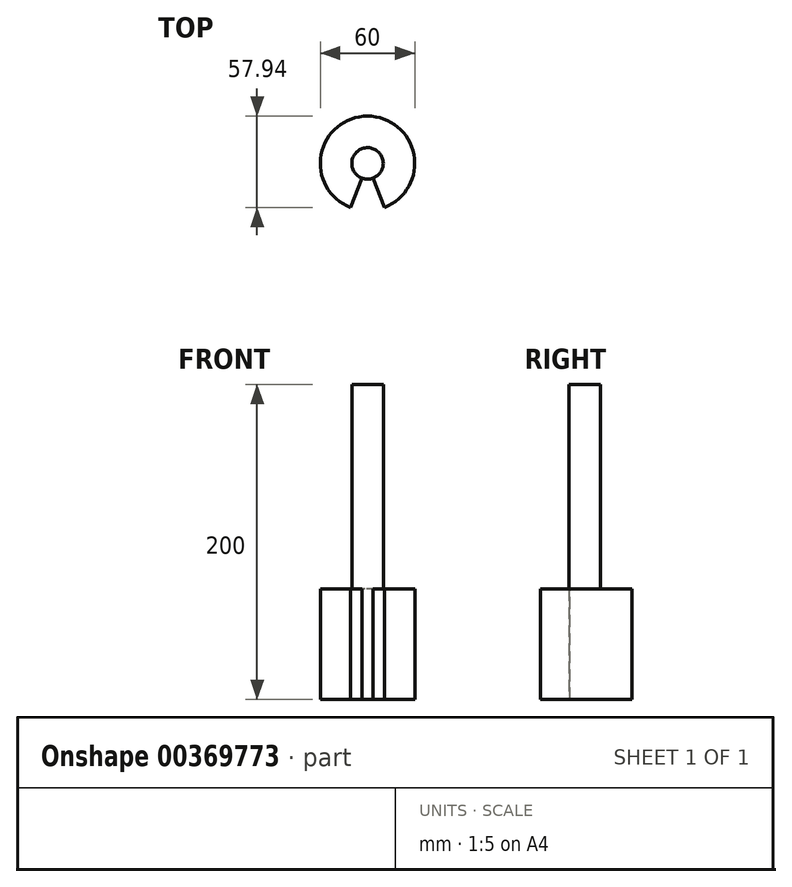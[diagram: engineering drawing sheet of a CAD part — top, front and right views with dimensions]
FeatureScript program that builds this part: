
annotation { "Feature Type Name" : "Feature", "Feature Type Description" : "" }
export const myFeature = defineFeature(function(context is Context, id is Id, definition is map)
    precondition{}
    {
        {
            var Q0;
            Q0=qCreatedBy(makeId("Top.planeOp"),FACE);
            var sketch = newSketch(context, id + "F0", { "sketchPlane" : qUnion([Q0])});
            skCircle(sketch, "E0", {"center": v(0, 0) * mm, "radius": 30 * mm});
            skCircle(sketch, "E1", {"center": v(0, 0) * mm, "radius": 10 * mm});
            skSolve(sketch);
        }
        {
            var Q0;
            Q0=makeQuery(id+"F0.imprint","IMPRINT",FACE,{"disambiguationData":[TD([[makeQuery(id+"F0.imprint","IMPRINT",EDGE,{"derivedFrom":sQuery(id+"F0.wireOp",EDGE,"E0")}),1.0]])]});
            extrude(context, id + "F1", {"entities" : qUnion([Q0]), "depth" : 70 * mm, "offsetDistance" : 25 * mm});
        }
        {
            var Q0;
            Q0=makeQuery(id+"F1.opExtrude","CAP_FACE",FACE,{"disambiguationData":[OSD([sQuery(id+"F0.wireOp",EDGE,"E0")])],"isStart":false});
            var sketch = newSketch(context, id + "F2", { "sketchPlane" : qUnion([Q0])});
            skCircle(sketch, "E2", {"center": v(0, 0) * mm, "radius": 10 * mm});
            skSolve(sketch);
        }
        {
            var Q0;
            Q0=makeQuery(id+"F2.imprint","IMPRINT",FACE,{"disambiguationData":[TD([[makeQuery(id+"F2.imprint","IMPRINT",EDGE,{"derivedFrom":sQuery(id+"F2.wireOp",EDGE,"E2")}),1.0]])]});
            extrude(context, id + "F3", {"entities" : qUnion([Q0]), "operationType" : NewBodyOperationType.ADD, "depth" : 130 * mm, "offsetDistance" : 25 * mm, "hasSecondDirection" : true, "secondDirectionOppositeDirection" : true, "secondDirectionDepth" : 70 * mm});
        }
        {
            var Q0;
            Q0=makeQuery(id+"F1.opExtrude","CAP_FACE",FACE,{"disambiguationData":[OSD([sQuery(id+"F0.wireOp",EDGE,"E0"),sQuery(id+"F0.wireOp",EDGE,"E1")])],"isStart":false});
            var sketch = newSketch(context, id + "F4", { "sketchPlane" : qUnion([Q0])});
            skLineSegment(sketch, "E3", {"start": v(-3.43, -9.4) * mm, "end": v(-10.94, -27.94) * mm});
            skLineSegment(sketch, "E4.MirrorCS", {"start": v(3.43, -9.4) * mm, "end": v(10.94, -27.94) * mm});
            skSolve(sketch);
        }
        {
            var Q0;
            {var subQ0=sQuery(id+"F4.wireOp",EDGE,"E3");Q0=makeQuery(id+"F4.imprint","IMPRINT",FACE,{"disambiguationData":[TD([[makeQuery(id+"F4.imprint","IMPRINT",EDGE,{"derivedFrom":subQ0}),1.0]])]});}
            extrude(context, id + "F5", {"entities" : qUnion([Q0]), "operationType" : NewBodyOperationType.REMOVE, "endBound" : BoundingType.UP_TO_NEXT, "oppositeDirection" : true, "depth" : 62.2 * mm, "offsetDistance" : 25 * mm});
        }
    });
